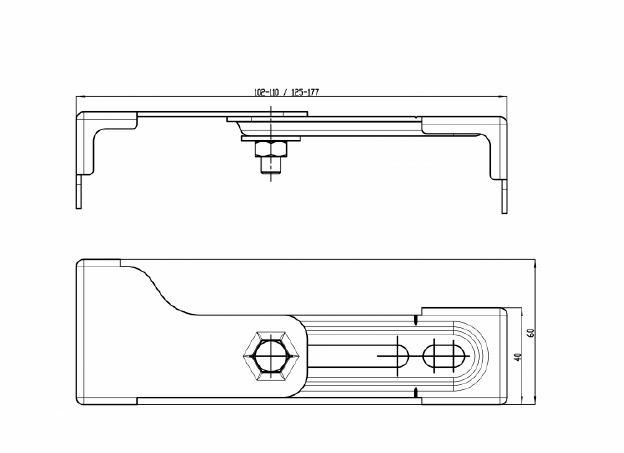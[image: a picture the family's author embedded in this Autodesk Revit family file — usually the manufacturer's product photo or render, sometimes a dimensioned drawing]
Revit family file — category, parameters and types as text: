
# Revit family: PRD_AR_PrplmbInstlFrm_InstallationFrameForUrinal_AQFX0001,AQFX0002
name_source: partatom
category: Plumbing Fixtures
revit_build: Autodesk Revit 2018 (Build: 20190510_1515(x64)
units: mm (PartAtom-declared; Revit-internal decimal feet)

## family parameters
Always vertical = Yes
Cut with Voids When Loaded = Yes
OmniClass Number = 23.40.20.00
OmniClass Title = General Furniture and Specialties
Part Type = Normal
Room Calculation Point = No
Round Connector Dimension = Use Diameter
Shared = Yes
Work Plane-Based = No

## types (2) — shared parameters
AssetType = Fixed
Category = Pr_40_20_93_62, Pre-plumbed installation frames
CisternCapacity = 0
CisternHeight = None
DiameterNominal = 15  [stored 0.0492126 ft]
DurationUnit = year
Finish = powder coated
FlushRate = 0
FlushType = Unset
Form = Installation frame
FrameMaterial = PRD_AR_StainlessSteel_Colored
HeightAdjustment = 200 mm  [stored 0.656168 ft]
IfcExportAs = IfcSanitaryTerminalType
IfcExportType = CISTERN
InletSize = DN 15 (1/2 inch.)
IsAutomaticFlush = 0
IsSingleFlush = 0
Manufacturer = KWC Group AG
ManufacturerName = KWC Group AG
ManufacturerURL = www.kwc.com
Materials = powder coated steel
NBSDescription = Preplumbed installation frames
NBSReference = 45-35-70/421
NominalLength = 135 mm
NominalWidth = 525 mm
OutletOffset = 100 mm  [stored 0.328084 ft]
OutletOffsetVertical = 100 mm  [stored 0.328084 ft]
OutletSize = DN 50 (2 inch.)
PipeMaterial = PRD_AR_OutletPipe
ProductInformation = https://pim.kwc.com
SteelMaterial = PRD_AR_StainlessSteel_SatinFinished
URL = www.kwc.com
Uniclass2015Code = Pr_40_20_93_62
Uniclass2015Title = Pre-plumbed installation frames
Uniclass2015Version = Products v1.10
Version = 1
WarrantyDurationUnit = year
WasteSize = 50  [stored 0.164042 ft]

## per-type parameters (varying)
| type | 3rdBeamOffset | AdditionalBeam | BIMObjectName | Description | Features | GrossWeight | ModelNumber | Name | NetWeight | NominalHeight | OverallHeight | Size |
| AQFX0002 | 1199 mm | Yes | PRD_AR_PreplumbedInstallationFrames_InstallationFrameForUrinal_AQFX0002 | AQUAFIX installation frame for stainless steel urinals, with pre-mounted basic installation kit for in-wall urinal flush valves FLUSH-S and FLUSH-C. Self-supporting, powder coated, steel-frame construction, TÜV-tested, for individual mounting for dry-wall lining, height-adjustable traverse beam for fastening urinal, fitting connection and outlet mount, pre-mounted for urinal CMPX538, sound-insulated wall duct G 1/2, universal outlet bend DN 50, urinal fastening bolts, building protection and fastening material. | steel, wall and floor mounting, 525x1440x135 mm (WxHxD) | 14.00 kg | 2000110549 | AQUAFIX urinal installation frame for stainless steel urinals AQFX0002 | 13.30 kg | 1440 mm | 1440 mm | 525x1440x135 mm |
| AQFX0001 | 1019.5 mm  [stored 3.34482 ft] | No | PRD_AR_PreplumbedInstallationFrames_InstallationFrameForUrinal_AQFX0001 | AQUAFIX installation frame for ceramic urinals, with pre-mounted basic installation kit for in-wall urinal flush valves FLUSH-S and

FLUSH-C. Self-supporting, powder coated, steel-frame construction, TÜV-tested, for individual mounting for dry-wall lining, height-
adjustable traverse beam for fastening urinal, fitting connection and outlet mount, sound-insulated wall duct with flush connector,

universal outlet bend DN 50, urinal fastening bolts, building protection and fastening material. | steel, wall and floor mounting, 525x1120x135 mm (WxHxD) | 10.80 kg | 2030020123 | AQUAFIX urinal installation frame for stainless steel urinals AQFX0001 | 10.26 kg | 1120 mm  [stored 3.67454 ft] | 1120 mm  [stored 3.67454 ft] | 525x1120x135 mm |

note: column(s) folded — value = type name in every type: Model, ModelReference

note: [stored X ft] marks values corroborated as IEEE doubles in the binary element streams (Revit-internal decimal feet)

## geometry (parser evidence)
native form markers: Sweep x14
no freeform markers — native parametric forms only
